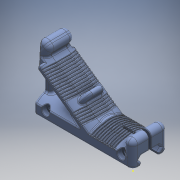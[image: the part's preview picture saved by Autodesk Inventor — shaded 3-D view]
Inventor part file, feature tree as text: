
AUTODESK INVENTOR PART (.ipt)
format: ipt  version: 2016 (Build 200138000, 138)  size: 6,654,464 bytes
history: native  units: mm
features: other x3, sketch x1
ambient origin geometry x8: Origin, YZ Plane, XZ Plane, XY Plane, X Axis, Y Axis, Z Axis, Center Point
bodies: Solid1 (feature_tree)
feature tree (4):
  other  "afg v2 short 2.ipt"
  other  "Solid1::afg v2 short 2.ipt"
  other  "TaggingFeature2"
  sketch  "Sketch9"  dims[d1=100.0mm]
